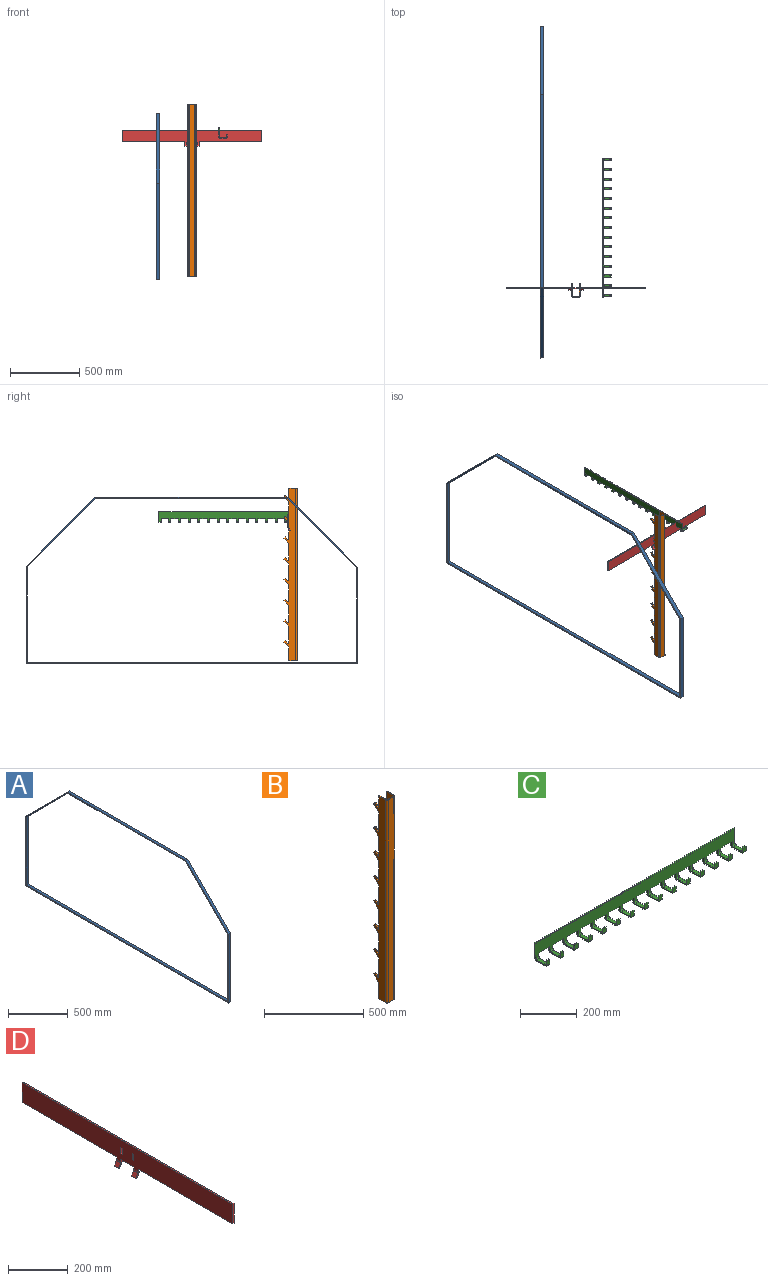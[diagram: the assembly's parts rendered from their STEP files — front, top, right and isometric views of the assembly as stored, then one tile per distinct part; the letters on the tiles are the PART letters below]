
ASSEMBLY  parts=4 mates=6
PART A: 14 faces, bbox 25x2400x1205 mm
  f0: plane 1397.07x25mm, normal (0,0,1), area 34926.8mm2, adj f1,f11,f12,f13
  f1: plane 505x505mm, normal (0,-0.71,0.71), area 17854.4mm2, adj f0,f2,f12,f13
  f2: plane 700x25mm, normal (0,-1,0), area 17500mm2, adj f1,f3,f12,f13
  f3: plane 2400x25mm, normal (0,0,-1), area 60000mm2, adj f2,f4,f12,f13
  f4: plane 707.07x25mm, normal (0,1,0), area 17676.8mm2, adj f3,f11,f12,f13
  f5: plane 2380x25mm, normal (0,0,1), area 59500mm2, adj f6,f10,f12,f13
  f6: plane 685.86x25mm, normal (0,1,0), area 17146.4mm2, adj f5,f7,f12,f13
  f7: plane 499.14x499.14mm, normal (0,0.71,-0.71), area 17647.3mm2, adj f6,f8,f12,f13
  f8: plane 1388.79x25mm, normal (0,0,-1), area 34719.7mm2, adj f7,f9,f12,f13
  f9: plane 492.07x492.07mm, normal (0,-0.71,-0.71), area 17397.3mm2, adj f8,f10,f12,f13
  f10: plane 692.93x25mm, normal (0,-1,0), area 17323.2mm2, adj f5,f9,f12,f13
  f11: plane 497.93x497.93mm, normal (0,0.71,0.71), area 17604.4mm2, adj f0,f4,f12,f13
  f12: plane 2400x1205mm, normal (1,0,0), area 65859.3mm2, adj f0,f1,f2,f3,f4,f5,f6,f7
  f13: plane 2400x1205mm, normal (-1,0,0), area 65859.3mm2, adj f0,f1,f2,f3,f4,f5,f6,f7
PART B: 134 faces, bbox 60x95.4x1250 mm
  f0: plane 100.89x5mm, normal (0,1,0), area 504.4mm2, adj f18,f20,f29,f122
  f1: plane 100.89x5mm, normal (0,1,0), area 504.4mm2, adj f24,f26,f29,f116
  f2: plane 122.79x5mm, normal (0,1,0), area 613.9mm2, adj f18,f20,f110,f120
  f3: plane 122.79x5mm, normal (0,1,0), area 613.9mm2, adj f24,f26,f104,f115
  f4: plane 122.79x5mm, normal (0,1,0), area 613.9mm2, adj f18,f20,f98,f108
  f5: plane 122.79x5mm, normal (0,1,0), area 613.9mm2, adj f24,f26,f92,f103
  f6: plane 122.79x5mm, normal (0,1,0), area 613.9mm2, adj f18,f20,f86,f96
  f7: plane 122.79x5mm, normal (0,1,0), area 613.9mm2, adj f24,f26,f80,f91
  f8: plane 122.79x5mm, normal (0,1,0), area 613.9mm2, adj f18,f20,f74,f84
  f9: plane 122.79x5mm, normal (0,1,0), area 613.9mm2, adj f24,f26,f68,f79
  f10: plane 122.79x5mm, normal (0,1,0), area 613.9mm2, adj f18,f20,f62,f72
  f11: plane 122.79x5mm, normal (0,1,0), area 613.9mm2, adj f24,f26,f56,f67
  f12: plane 122.79x5mm, normal (0,1,0), area 613.9mm2, adj f18,f20,f50,f60
  f13: plane 122.79x5mm, normal (0,1,0), area 613.9mm2, adj f24,f26,f44,f55
  f14: plane 122.79x5mm, normal (0,1,0), area 613.9mm2, adj f18,f20,f38,f48
  f15: plane 122.79x5mm, normal (0,1,0), area 613.9mm2, adj f24,f26,f32,f43
  f16: plane 1250x40mm, normal (0,1,0), area 50000mm2, adj f17,f27,f28,f29
  f17: cylinder r=5mm len=1250mm, axis (0,0,-1), area 9817.5mm2, adj f16,f18,f28,f29
  f18: plane 1250x50mm, normal (1,0,0), area 62500mm2, adj f0,f2,f4,f6,f8,f10,f12,f14
  f19: plane 71.9x5mm, normal (0,1,0), area 359.5mm2, adj f18,f20,f28,f36
  f20: plane 1250x84.36mm, normal (-1,0,0), area 66472.5mm2, adj f0,f2,f4,f6,f8,f10,f12,f14
  f21: cylinder r=11mm len=1250mm, axis (0,0,-1), area 21598.4mm2, adj f20,f22,f28,f29
  f22: plane 1250x38mm, normal (0,-1,0), area 47500mm2, adj f21,f23,f28,f29
  f23: cylinder r=11mm len=1250mm, axis (0,0,-1), area 21598.4mm2, adj f22,f24,f28,f29
  f24: plane 1250x84.36mm, normal (1,0,0), area 66472.5mm2, adj f1,f3,f5,f7,f9,f11,f13,f15
  f25: plane 71.9x5mm, normal (0,1,0), area 359.5mm2, adj f24,f26,f28,f31
  f26: plane 1250x50mm, normal (-1,0,0), area 62500mm2, adj f1,f3,f5,f7,f9,f11,f13,f15
  f27: cylinder r=5mm len=1250mm, axis (0,0,-1), area 9817.5mm2, adj f16,f26,f28,f29
  f28: plane 60x60mm, normal (0,0,1), area 808.8mm2, adj f16,f17,f18,f19,f20,f21,f22,f23
  f29: plane 60x60mm, normal (0,0,-1), area 808.8mm2, adj f0,f1,f16,f17,f18,f20,f21,f22
  f30: plane 27.21x1mm, normal (0,-1,0), area 27.2mm2, adj f26,f31,f32,f35
  f31: plane 6x6mm, normal (0,0,1), area 36mm2, adj f24,f25,f30,f34,f35
  f32: plane 31.82x31.82mm, normal (0,0.71,-0.71), area 270mm2, adj f15,f24,f30,f35,f132
  f33: plane 6x3.54mm, normal (0,0.71,0.71), area 30mm2, adj f24,f35,f132,f133
  f34: plane 15.21x15.21mm, normal (0,-0.71,0.71), area 129.1mm2, adj f24,f31,f35,f133
  f35: plane 43.89x33.28mm, normal (-1,0,0), area 644.8mm2, adj f30,f31,f32,f33,f34,f132,f133
  f36: plane 6x6mm, normal (0,0,1), area 36mm2, adj f19,f20,f37,f40,f41
  f37: plane 27.21x1mm, normal (0,-1,0), area 27.2mm2, adj f18,f36,f38,f41
  f38: plane 31.82x31.82mm, normal (0,0.71,-0.71), area 270mm2, adj f14,f20,f37,f41,f130
  f39: plane 6x3.54mm, normal (0,0.71,0.71), area 30mm2, adj f20,f41,f130,f131
  f40: plane 15.21x15.21mm, normal (0,-0.71,0.71), area 129.1mm2, adj f20,f36,f41,f131
  f41: plane 43.89x33.28mm, normal (1,0,0), area 644.8mm2, adj f36,f37,f38,f39,f40,f130,f131
  f42: plane 27.21x1mm, normal (0,-1,0), area 27.2mm2, adj f26,f43,f44,f47
  f43: plane 6x6mm, normal (0,0,1), area 36mm2, adj f15,f24,f42,f46,f47
  f44: plane 31.82x31.82mm, normal (0,0.71,-0.71), area 270mm2, adj f13,f24,f42,f47,f128
  f45: plane 6x3.54mm, normal (0,0.71,0.71), area 30mm2, adj f24,f47,f128,f129
  f46: plane 15.21x15.21mm, normal (0,-0.71,0.71), area 129.1mm2, adj f24,f43,f47,f129
  f47: plane 43.89x33.28mm, normal (-1,0,0), area 644.8mm2, adj f42,f43,f44,f45,f46,f128,f129
  f48: plane 6x6mm, normal (0,0,1), area 36mm2, adj f14,f20,f49,f52,f53
  f49: plane 27.21x1mm, normal (0,-1,0), area 27.2mm2, adj f18,f48,f50,f53
  f50: plane 31.82x31.82mm, normal (0,0.71,-0.71), area 270mm2, adj f12,f20,f49,f53,f126
  f51: plane 6x3.54mm, normal (0,0.71,0.71), area 30mm2, adj f20,f53,f126,f127
  f52: plane 15.21x15.21mm, normal (0,-0.71,0.71), area 129.1mm2, adj f20,f48,f53,f127
  f53: plane 43.89x33.28mm, normal (1,0,0), area 644.8mm2, adj f48,f49,f50,f51,f52,f126,f127
  f54: plane 27.21x1mm, normal (0,-1,0), area 27.2mm2, adj f26,f55,f56,f59
  f55: plane 6x6mm, normal (0,0,1), area 36mm2, adj f13,f24,f54,f58,f59
  f56: plane 35.36x35.36mm, normal (0,0.71,-0.71), area 300mm2, adj f11,f24,f54,f57,f59
  f57: plane 10.61x10.61mm, normal (0,0.71,0.71), area 90mm2, adj f24,f56,f58,f59
  f58: plane 18.75x18.75mm, normal (0,-0.71,0.71), area 159.1mm2, adj f24,f55,f57,f59
  f59: plane 45.96x35.36mm, normal (-1,0,0), area 655.5mm2, adj f54,f55,f56,f57,f58
  f60: plane 6x6mm, normal (0,0,1), area 36mm2, adj f12,f20,f61,f64,f65
  f61: plane 27.21x1mm, normal (0,-1,0), area 27.2mm2, adj f18,f60,f62,f65
  f62: plane 35.36x35.36mm, normal (0,0.71,-0.71), area 300mm2, adj f10,f20,f61,f63,f65
  f63: plane 10.61x10.61mm, normal (0,0.71,0.71), area 90mm2, adj f20,f62,f64,f65
  f64: plane 18.75x18.75mm, normal (0,-0.71,0.71), area 159.1mm2, adj f20,f60,f63,f65
  f65: plane 45.96x35.36mm, normal (1,0,0), area 655.5mm2, adj f60,f61,f62,f63,f64
  f66: plane 27.21x1mm, normal (0,-1,0), area 27.2mm2, adj f26,f67,f68,f71
  f67: plane 6x6mm, normal (0,0,1), area 36mm2, adj f11,f24,f66,f70,f71
  f68: plane 35.36x35.36mm, normal (0,0.71,-0.71), area 300mm2, adj f9,f24,f66,f69,f71
  f69: plane 10.61x10.61mm, normal (0,0.71,0.71), area 90mm2, adj f24,f68,f70,f71
  f70: plane 18.75x18.75mm, normal (0,-0.71,0.71), area 159.1mm2, adj f24,f67,f69,f71
  f71: plane 45.96x35.36mm, normal (-1,0,0), area 655.5mm2, adj f66,f67,f68,f69,f70
  f72: plane 6x6mm, normal (0,0,1), area 36mm2, adj f10,f20,f73,f76,f77
  f73: plane 27.21x1mm, normal (0,-1,0), area 27.2mm2, adj f18,f72,f74,f77
  f74: plane 35.36x35.36mm, normal (0,0.71,-0.71), area 300mm2, adj f8,f20,f73,f75,f77
  f75: plane 10.61x10.61mm, normal (0,0.71,0.71), area 90mm2, adj f20,f74,f76,f77
  f76: plane 18.75x18.75mm, normal (0,-0.71,0.71), area 159.1mm2, adj f20,f72,f75,f77
  f77: plane 45.96x35.36mm, normal (1,0,0), area 655.5mm2, adj f72,f73,f74,f75,f76
  f78: plane 27.21x1mm, normal (0,-1,0), area 27.2mm2, adj f26,f79,f80,f83
  f79: plane 6x6mm, normal (0,0,1), area 36mm2, adj f9,f24,f78,f82,f83
  f80: plane 35.36x35.36mm, normal (0,0.71,-0.71), area 300mm2, adj f7,f24,f78,f81,f83
  f81: plane 10.61x10.61mm, normal (0,0.71,0.71), area 90mm2, adj f24,f80,f82,f83
  f82: plane 18.75x18.75mm, normal (0,-0.71,0.71), area 159.1mm2, adj f24,f79,f81,f83
  f83: plane 45.96x35.36mm, normal (-1,0,0), area 655.5mm2, adj f78,f79,f80,f81,f82
  f84: plane 6x6mm, normal (0,0,1), area 36mm2, adj f8,f20,f85,f88,f89
  f85: plane 27.21x1mm, normal (0,-1,0), area 27.2mm2, adj f18,f84,f86,f89
  f86: plane 35.36x35.36mm, normal (0,0.71,-0.71), area 300mm2, adj f6,f20,f85,f87,f89
  f87: plane 10.61x10.61mm, normal (0,0.71,0.71), area 90mm2, adj f20,f86,f88,f89
  f88: plane 18.75x18.75mm, normal (0,-0.71,0.71), area 159.1mm2, adj f20,f84,f87,f89
  f89: plane 45.96x35.36mm, normal (1,0,0), area 655.5mm2, adj f84,f85,f86,f87,f88
  f90: plane 27.21x1mm, normal (0,-1,0), area 27.2mm2, adj f26,f91,f92,f95
  f91: plane 6x6mm, normal (0,0,1), area 36mm2, adj f7,f24,f90,f94,f95
  f92: plane 35.36x35.36mm, normal (0,0.71,-0.71), area 300mm2, adj f5,f24,f90,f93,f95
  f93: plane 10.61x10.61mm, normal (0,0.71,0.71), area 90mm2, adj f24,f92,f94,f95
  f94: plane 18.75x18.75mm, normal (0,-0.71,0.71), area 159.1mm2, adj f24,f91,f93,f95
  f95: plane 45.96x35.36mm, normal (-1,0,0), area 655.5mm2, adj f90,f91,f92,f93,f94
  f96: plane 6x6mm, normal (0,0,1), area 36mm2, adj f6,f20,f97,f100,f101
  f97: plane 27.21x1mm, normal (0,-1,0), area 27.2mm2, adj f18,f96,f98,f101
  f98: plane 35.36x35.36mm, normal (0,0.71,-0.71), area 300mm2, adj f4,f20,f97,f99,f101
  f99: plane 10.61x10.61mm, normal (0,0.71,0.71), area 90mm2, adj f20,f98,f100,f101
  f100: plane 18.75x18.75mm, normal (0,-0.71,0.71), area 159.1mm2, adj f20,f96,f99,f101
  f101: plane 45.96x35.36mm, normal (1,0,0), area 655.5mm2, adj f96,f97,f98,f99,f100
  f102: plane 27.21x1mm, normal (0,-1,0), area 27.2mm2, adj f26,f103,f104,f107
  f103: plane 6x6mm, normal (0,0,1), area 36mm2, adj f5,f24,f102,f106,f107
  f104: plane 35.36x35.36mm, normal (0,0.71,-0.71), area 300mm2, adj f3,f24,f102,f105,f107
  f105: plane 10.61x10.61mm, normal (0,0.71,0.71), area 90mm2, adj f24,f104,f106,f107
  f106: plane 18.75x18.75mm, normal (0,-0.71,0.71), area 159.1mm2, adj f24,f103,f105,f107
  f107: plane 45.96x35.36mm, normal (-1,0,0), area 655.5mm2, adj f102,f103,f104,f105,f106
  f108: plane 6x6mm, normal (0,0,1), area 36mm2, adj f4,f20,f109,f112,f113
  f109: plane 27.21x1mm, normal (0,-1,0), area 27.2mm2, adj f18,f108,f110,f113
  f110: plane 35.36x35.36mm, normal (0,0.71,-0.71), area 300mm2, adj f2,f20,f109,f111,f113
  f111: plane 10.61x10.61mm, normal (0,0.71,0.71), area 90mm2, adj f20,f110,f112,f113
  f112: plane 18.75x18.75mm, normal (0,-0.71,0.71), area 159.1mm2, adj f20,f108,f111,f113
  f113: plane 45.96x35.36mm, normal (1,0,0), area 655.5mm2, adj f108,f109,f110,f111,f112
  f114: plane 27.21x1mm, normal (0,-1,0), area 27.2mm2, adj f26,f115,f116,f119
  f115: plane 6x6mm, normal (0,0,1), area 36mm2, adj f3,f24,f114,f118,f119
  f116: plane 35.36x35.36mm, normal (0,0.71,-0.71), area 300mm2, adj f1,f24,f114,f117,f119
  f117: plane 10.61x10.61mm, normal (0,0.71,0.71), area 90mm2, adj f24,f116,f118,f119
  f118: plane 18.75x18.75mm, normal (0,-0.71,0.71), area 159.1mm2, adj f24,f115,f117,f119
  f119: plane 45.96x35.36mm, normal (-1,0,0), area 655.5mm2, adj f114,f115,f116,f117,f118
  f120: plane 6x6mm, normal (0,0,1), area 36mm2, adj f2,f20,f121,f124,f125
  f121: plane 27.21x1mm, normal (0,-1,0), area 27.2mm2, adj f18,f120,f122,f125
  f122: plane 35.36x35.36mm, normal (0,0.71,-0.71), area 300mm2, adj f0,f20,f121,f123,f125
  f123: plane 10.61x10.61mm, normal (0,0.71,0.71), area 90mm2, adj f20,f122,f124,f125
  f124: plane 18.75x18.75mm, normal (0,-0.71,0.71), area 159.1mm2, adj f20,f120,f123,f125
  f125: plane 45.96x35.36mm, normal (1,0,0), area 655.5mm2, adj f120,f121,f122,f123,f124
  f126: cylinder r=5mm len=7.07mm, axis (1,0,0), area 47.1mm2, adj f20,f50,f51,f53
  f127: cylinder r=5mm len=7.07mm, axis (1,0,0), area 47.1mm2, adj f20,f51,f52,f53
  f128: cylinder r=5mm len=7.07mm, axis (1,0,0), area 47.1mm2, adj f24,f44,f45,f47
  f129: cylinder r=5mm len=7.07mm, axis (1,0,0), area 47.1mm2, adj f24,f45,f46,f47
  f130: cylinder r=5mm len=7.07mm, axis (1,0,0), area 47.1mm2, adj f20,f38,f39,f41
  f131: cylinder r=5mm len=7.07mm, axis (1,0,0), area 47.1mm2, adj f20,f39,f40,f41
  f132: cylinder r=5mm len=7.07mm, axis (1,0,0), area 47.1mm2, adj f24,f32,f33,f35
  f133: cylinder r=5mm len=7.07mm, axis (1,0,0), area 47.1mm2, adj f24,f33,f34,f35
PART C: 184 faces, bbox 1000x60x75 mm
  f0: plane 5x5mm, normal (0,0,-1), area 25mm2, adj f16,f18,f19,f182
  f1: plane 55x5mm, normal (0,0,-1), area 275mm2, adj f18,f19,f171,f183
  f2: plane 55x5mm, normal (0,0,-1), area 275mm2, adj f18,f19,f160,f172
  f3: plane 55x5mm, normal (0,0,-1), area 275mm2, adj f18,f19,f149,f161
  f4: plane 55x5mm, normal (0,0,-1), area 275mm2, adj f18,f19,f138,f150
  f5: plane 55x5mm, normal (0,0,-1), area 275mm2, adj f18,f19,f127,f139
  f6: plane 55x5mm, normal (0,0,-1), area 275mm2, adj f18,f19,f116,f128
  f7: plane 55x5mm, normal (0,0,-1), area 275mm2, adj f18,f19,f105,f117
  f8: plane 55x5mm, normal (0,0,-1), area 275mm2, adj f18,f19,f94,f106
  f9: plane 55x5mm, normal (0,0,-1), area 275mm2, adj f18,f19,f83,f95
  f10: plane 55x5mm, normal (0,0,-1), area 275mm2, adj f18,f19,f72,f84
  f11: plane 55x5mm, normal (0,0,-1), area 275mm2, adj f18,f19,f61,f73
  f12: plane 55x5mm, normal (0,0,-1), area 275mm2, adj f18,f19,f50,f62
  f13: plane 55x5mm, normal (0,0,-1), area 275mm2, adj f18,f19,f39,f51
  f14: plane 55x5mm, normal (0,0,-1), area 275mm2, adj f18,f19,f29,f40
  f15: plane 1000x5mm, normal (0,0,1), area 5000mm2, adj f16,f17,f18,f19
  f16: plane 50x5mm, normal (-1,0,0), area 250mm2, adj f0,f15,f18,f19
  f17: plane 75x60mm, normal (1,0,0), area 750mm2, adj f15,f18,f19,f20,f21,f22,f23,f24
  f18: plane 1000x65mm, normal (0,-1,0), area 53375mm2, adj f0,f1,f2,f3,f4,f5,f6,f7
  f19: plane 1000x70mm, normal (0,1,0), area 54500mm2, adj f0,f1,f2,f3,f4,f5,f6,f7
  f20: cylinder r=5mm len=15mm, axis (1,0,0), area 117.8mm2, adj f17,f19,f28,f29
  f21: cylinder r=5mm len=15mm, axis (1,0,0), area 117.8mm2, adj f17,f18,f22,f29
  f22: plane 40x15mm, normal (0,0,1), area 600mm2, adj f17,f21,f23,f29
  f23: cylinder r=5mm len=15mm, axis (1,0,0), area 117.8mm2, adj f17,f22,f24,f29
  f24: plane 15x15mm, normal (0,1,0), area 225mm2, adj f17,f23,f25,f29
  f25: plane 15x5mm, normal (0,0,1), area 75mm2, adj f17,f24,f26,f29
  f26: plane 20x15mm, normal (0,-1,0), area 300mm2, adj f17,f25,f27,f29
  f27: cylinder r=5mm len=15mm, axis (1,0,0), area 117.8mm2, adj f17,f26,f28,f29
  f28: plane 50x15mm, normal (0,0,-1), area 750mm2, adj f17,f20,f27,f29
  f29: plane 60x25mm, normal (-1,0,0), area 500mm2, adj f14,f18,f19,f20,f21,f22,f23,f24
  f30: cylinder r=5mm len=15mm, axis (1,0,0), area 117.8mm2, adj f19,f38,f39,f40
  f31: cylinder r=5mm len=15mm, axis (1,0,0), area 117.8mm2, adj f18,f32,f39,f40
  f32: plane 40x15mm, normal (0,0,1), area 600mm2, adj f31,f33,f39,f40
  f33: cylinder r=5mm len=15mm, axis (1,0,0), area 117.8mm2, adj f32,f34,f39,f40
  f34: plane 15x15mm, normal (0,1,0), area 225mm2, adj f33,f35,f39,f40
  f35: plane 15x5mm, normal (0,0,1), area 75mm2, adj f34,f36,f39,f40
  f36: plane 20x15mm, normal (0,-1,0), area 300mm2, adj f35,f37,f39,f40
  f37: cylinder r=5mm len=15mm, axis (1,0,0), area 117.8mm2, adj f36,f38,f39,f40
  f38: plane 50x15mm, normal (0,0,-1), area 750mm2, adj f30,f37,f39,f40
  f39: plane 60x25mm, normal (-1,0,0), area 500mm2, adj f13,f18,f19,f30,f31,f32,f33,f34
  f40: plane 60x25mm, normal (1,0,0), area 500mm2, adj f14,f18,f19,f30,f31,f32,f33,f34
  f41: cylinder r=5mm len=15mm, axis (1,0,0), area 117.8mm2, adj f19,f49,f50,f51
  f42: cylinder r=5mm len=15mm, axis (1,0,0), area 117.8mm2, adj f18,f43,f50,f51
  f43: plane 40x15mm, normal (0,0,1), area 600mm2, adj f42,f44,f50,f51
  f44: cylinder r=5mm len=15mm, axis (1,0,0), area 117.8mm2, adj f43,f45,f50,f51
  f45: plane 15x15mm, normal (0,1,0), area 225mm2, adj f44,f46,f50,f51
  f46: plane 15x5mm, normal (0,0,1), area 75mm2, adj f45,f47,f50,f51
  f47: plane 20x15mm, normal (0,-1,0), area 300mm2, adj f46,f48,f50,f51
  f48: cylinder r=5mm len=15mm, axis (1,0,0), area 117.8mm2, adj f47,f49,f50,f51
  f49: plane 50x15mm, normal (0,0,-1), area 750mm2, adj f41,f48,f50,f51
  f50: plane 60x25mm, normal (-1,0,0), area 500mm2, adj f12,f18,f19,f41,f42,f43,f44,f45
  f51: plane 60x25mm, normal (1,0,0), area 500mm2, adj f13,f18,f19,f41,f42,f43,f44,f45
  f52: cylinder r=5mm len=15mm, axis (1,0,0), area 117.8mm2, adj f19,f60,f61,f62
  f53: cylinder r=5mm len=15mm, axis (1,0,0), area 117.8mm2, adj f18,f54,f61,f62
  f54: plane 40x15mm, normal (0,0,1), area 600mm2, adj f53,f55,f61,f62
  f55: cylinder r=5mm len=15mm, axis (1,0,0), area 117.8mm2, adj f54,f56,f61,f62
  f56: plane 15x15mm, normal (0,1,0), area 225mm2, adj f55,f57,f61,f62
  f57: plane 15x5mm, normal (0,0,1), area 75mm2, adj f56,f58,f61,f62
  f58: plane 20x15mm, normal (0,-1,0), area 300mm2, adj f57,f59,f61,f62
  f59: cylinder r=5mm len=15mm, axis (1,0,0), area 117.8mm2, adj f58,f60,f61,f62
  f60: plane 50x15mm, normal (0,0,-1), area 750mm2, adj f52,f59,f61,f62
  f61: plane 60x25mm, normal (-1,0,0), area 500mm2, adj f11,f18,f19,f52,f53,f54,f55,f56
  f62: plane 60x25mm, normal (1,0,0), area 500mm2, adj f12,f18,f19,f52,f53,f54,f55,f56
  f63: cylinder r=5mm len=15mm, axis (1,0,0), area 117.8mm2, adj f19,f71,f72,f73
  f64: cylinder r=5mm len=15mm, axis (1,0,0), area 117.8mm2, adj f18,f65,f72,f73
  f65: plane 40x15mm, normal (0,0,1), area 600mm2, adj f64,f66,f72,f73
  f66: cylinder r=5mm len=15mm, axis (1,0,0), area 117.8mm2, adj f65,f67,f72,f73
  f67: plane 15x15mm, normal (0,1,0), area 225mm2, adj f66,f68,f72,f73
  f68: plane 15x5mm, normal (0,0,1), area 75mm2, adj f67,f69,f72,f73
  f69: plane 20x15mm, normal (0,-1,0), area 300mm2, adj f68,f70,f72,f73
  f70: cylinder r=5mm len=15mm, axis (1,0,0), area 117.8mm2, adj f69,f71,f72,f73
  f71: plane 50x15mm, normal (0,0,-1), area 750mm2, adj f63,f70,f72,f73
  f72: plane 60x25mm, normal (-1,0,0), area 500mm2, adj f10,f18,f19,f63,f64,f65,f66,f67
  f73: plane 60x25mm, normal (1,0,0), area 500mm2, adj f11,f18,f19,f63,f64,f65,f66,f67
  f74: cylinder r=5mm len=15mm, axis (1,0,0), area 117.8mm2, adj f19,f82,f83,f84
  f75: cylinder r=5mm len=15mm, axis (1,0,0), area 117.8mm2, adj f18,f76,f83,f84
  f76: plane 40x15mm, normal (0,0,1), area 600mm2, adj f75,f77,f83,f84
  f77: cylinder r=5mm len=15mm, axis (1,0,0), area 117.8mm2, adj f76,f78,f83,f84
  f78: plane 15x15mm, normal (0,1,0), area 225mm2, adj f77,f79,f83,f84
  f79: plane 15x5mm, normal (0,0,1), area 75mm2, adj f78,f80,f83,f84
  f80: plane 20x15mm, normal (0,-1,0), area 300mm2, adj f79,f81,f83,f84
  f81: cylinder r=5mm len=15mm, axis (1,0,0), area 117.8mm2, adj f80,f82,f83,f84
  f82: plane 50x15mm, normal (0,0,-1), area 750mm2, adj f74,f81,f83,f84
  f83: plane 60x25mm, normal (-1,0,0), area 500mm2, adj f9,f18,f19,f74,f75,f76,f77,f78
  f84: plane 60x25mm, normal (1,0,0), area 500mm2, adj f10,f18,f19,f74,f75,f76,f77,f78
  f85: cylinder r=5mm len=15mm, axis (1,0,0), area 117.8mm2, adj f19,f93,f94,f95
  f86: cylinder r=5mm len=15mm, axis (1,0,0), area 117.8mm2, adj f18,f87,f94,f95
  f87: plane 40x15mm, normal (0,0,1), area 600mm2, adj f86,f88,f94,f95
  f88: cylinder r=5mm len=15mm, axis (1,0,0), area 117.8mm2, adj f87,f89,f94,f95
  f89: plane 15x15mm, normal (0,1,0), area 225mm2, adj f88,f90,f94,f95
  f90: plane 15x5mm, normal (0,0,1), area 75mm2, adj f89,f91,f94,f95
  f91: plane 20x15mm, normal (0,-1,0), area 300mm2, adj f90,f92,f94,f95
  f92: cylinder r=5mm len=15mm, axis (1,0,0), area 117.8mm2, adj f91,f93,f94,f95
  f93: plane 50x15mm, normal (0,0,-1), area 750mm2, adj f85,f92,f94,f95
  f94: plane 60x25mm, normal (-1,0,0), area 500mm2, adj f8,f18,f19,f85,f86,f87,f88,f89
  f95: plane 60x25mm, normal (1,0,0), area 500mm2, adj f9,f18,f19,f85,f86,f87,f88,f89
  f96: cylinder r=5mm len=15mm, axis (1,0,0), area 117.8mm2, adj f19,f104,f105,f106
  f97: cylinder r=5mm len=15mm, axis (1,0,0), area 117.8mm2, adj f18,f98,f105,f106
  f98: plane 40x15mm, normal (0,0,1), area 600mm2, adj f97,f99,f105,f106
  f99: cylinder r=5mm len=15mm, axis (1,0,0), area 117.8mm2, adj f98,f100,f105,f106
  f100: plane 15x15mm, normal (0,1,0), area 225mm2, adj f99,f101,f105,f106
  f101: plane 15x5mm, normal (0,0,1), area 75mm2, adj f100,f102,f105,f106
  f102: plane 20x15mm, normal (0,-1,0), area 300mm2, adj f101,f103,f105,f106
  f103: cylinder r=5mm len=15mm, axis (1,0,0), area 117.8mm2, adj f102,f104,f105,f106
  f104: plane 50x15mm, normal (0,0,-1), area 750mm2, adj f96,f103,f105,f106
  f105: plane 60x25mm, normal (-1,0,0), area 500mm2, adj f7,f18,f19,f96,f97,f98,f99,f100
  f106: plane 60x25mm, normal (1,0,0), area 500mm2, adj f8,f18,f19,f96,f97,f98,f99,f100
  f107: cylinder r=5mm len=15mm, axis (1,0,0), area 117.8mm2, adj f19,f115,f116,f117
  f108: cylinder r=5mm len=15mm, axis (1,0,0), area 117.8mm2, adj f18,f109,f116,f117
  f109: plane 40x15mm, normal (0,0,1), area 600mm2, adj f108,f110,f116,f117
  f110: cylinder r=5mm len=15mm, axis (1,0,0), area 117.8mm2, adj f109,f111,f116,f117
  f111: plane 15x15mm, normal (0,1,0), area 225mm2, adj f110,f112,f116,f117
  f112: plane 15x5mm, normal (0,0,1), area 75mm2, adj f111,f113,f116,f117
  f113: plane 20x15mm, normal (0,-1,0), area 300mm2, adj f112,f114,f116,f117
  f114: cylinder r=5mm len=15mm, axis (1,0,0), area 117.8mm2, adj f113,f115,f116,f117
  f115: plane 50x15mm, normal (0,0,-1), area 750mm2, adj f107,f114,f116,f117
  f116: plane 60x25mm, normal (-1,0,0), area 500mm2, adj f6,f18,f19,f107,f108,f109,f110,f111
  f117: plane 60x25mm, normal (1,0,0), area 500mm2, adj f7,f18,f19,f107,f108,f109,f110,f111
  f118: cylinder r=5mm len=15mm, axis (1,0,0), area 117.8mm2, adj f19,f126,f127,f128
  f119: cylinder r=5mm len=15mm, axis (1,0,0), area 117.8mm2, adj f18,f120,f127,f128
  f120: plane 40x15mm, normal (0,0,1), area 600mm2, adj f119,f121,f127,f128
  f121: cylinder r=5mm len=15mm, axis (1,0,0), area 117.8mm2, adj f120,f122,f127,f128
  f122: plane 15x15mm, normal (0,1,0), area 225mm2, adj f121,f123,f127,f128
  f123: plane 15x5mm, normal (0,0,1), area 75mm2, adj f122,f124,f127,f128
  f124: plane 20x15mm, normal (0,-1,0), area 300mm2, adj f123,f125,f127,f128
  f125: cylinder r=5mm len=15mm, axis (1,0,0), area 117.8mm2, adj f124,f126,f127,f128
  f126: plane 50x15mm, normal (0,0,-1), area 750mm2, adj f118,f125,f127,f128
  f127: plane 60x25mm, normal (-1,0,0), area 500mm2, adj f5,f18,f19,f118,f119,f120,f121,f122
  f128: plane 60x25mm, normal (1,0,0), area 500mm2, adj f6,f18,f19,f118,f119,f120,f121,f122
  f129: cylinder r=5mm len=15mm, axis (1,0,0), area 117.8mm2, adj f19,f137,f138,f139
  f130: cylinder r=5mm len=15mm, axis (1,0,0), area 117.8mm2, adj f18,f131,f138,f139
  f131: plane 40x15mm, normal (0,0,1), area 600mm2, adj f130,f132,f138,f139
  f132: cylinder r=5mm len=15mm, axis (1,0,0), area 117.8mm2, adj f131,f133,f138,f139
  f133: plane 15x15mm, normal (0,1,0), area 225mm2, adj f132,f134,f138,f139
  f134: plane 15x5mm, normal (0,0,1), area 75mm2, adj f133,f135,f138,f139
  f135: plane 20x15mm, normal (0,-1,0), area 300mm2, adj f134,f136,f138,f139
  f136: cylinder r=5mm len=15mm, axis (1,0,0), area 117.8mm2, adj f135,f137,f138,f139
  f137: plane 50x15mm, normal (0,0,-1), area 750mm2, adj f129,f136,f138,f139
  f138: plane 60x25mm, normal (-1,0,0), area 500mm2, adj f4,f18,f19,f129,f130,f131,f132,f133
  f139: plane 60x25mm, normal (1,0,0), area 500mm2, adj f5,f18,f19,f129,f130,f131,f132,f133
  f140: cylinder r=5mm len=15mm, axis (1,0,0), area 117.8mm2, adj f19,f148,f149,f150
  f141: cylinder r=5mm len=15mm, axis (1,0,0), area 117.8mm2, adj f18,f142,f149,f150
  f142: plane 40x15mm, normal (0,0,1), area 600mm2, adj f141,f143,f149,f150
  f143: cylinder r=5mm len=15mm, axis (1,0,0), area 117.8mm2, adj f142,f144,f149,f150
  f144: plane 15x15mm, normal (0,1,0), area 225mm2, adj f143,f145,f149,f150
  f145: plane 15x5mm, normal (0,0,1), area 75mm2, adj f144,f146,f149,f150
  f146: plane 20x15mm, normal (0,-1,0), area 300mm2, adj f145,f147,f149,f150
  f147: cylinder r=5mm len=15mm, axis (1,0,0), area 117.8mm2, adj f146,f148,f149,f150
  f148: plane 50x15mm, normal (0,0,-1), area 750mm2, adj f140,f147,f149,f150
  f149: plane 60x25mm, normal (-1,0,0), area 500mm2, adj f3,f18,f19,f140,f141,f142,f143,f144
  f150: plane 60x25mm, normal (1,0,0), area 500mm2, adj f4,f18,f19,f140,f141,f142,f143,f144
  f151: cylinder r=5mm len=15mm, axis (1,0,0), area 117.8mm2, adj f19,f159,f160,f161
  f152: cylinder r=5mm len=15mm, axis (1,0,0), area 117.8mm2, adj f18,f153,f160,f161
  f153: plane 40x15mm, normal (0,0,1), area 600mm2, adj f152,f154,f160,f161
  f154: cylinder r=5mm len=15mm, axis (1,0,0), area 117.8mm2, adj f153,f155,f160,f161
  f155: plane 15x15mm, normal (0,1,0), area 225mm2, adj f154,f156,f160,f161
  f156: plane 15x5mm, normal (0,0,1), area 75mm2, adj f155,f157,f160,f161
  f157: plane 20x15mm, normal (0,-1,0), area 300mm2, adj f156,f158,f160,f161
  f158: cylinder r=5mm len=15mm, axis (1,0,0), area 117.8mm2, adj f157,f159,f160,f161
  f159: plane 50x15mm, normal (0,0,-1), area 750mm2, adj f151,f158,f160,f161
  f160: plane 60x25mm, normal (-1,0,0), area 500mm2, adj f2,f18,f19,f151,f152,f153,f154,f155
  f161: plane 60x25mm, normal (1,0,0), area 500mm2, adj f3,f18,f19,f151,f152,f153,f154,f155
  f162: cylinder r=5mm len=15mm, axis (1,0,0), area 117.8mm2, adj f19,f170,f171,f172
  f163: cylinder r=5mm len=15mm, axis (1,0,0), area 117.8mm2, adj f18,f164,f171,f172
  f164: plane 40x15mm, normal (0,0,1), area 600mm2, adj f163,f165,f171,f172
  f165: cylinder r=5mm len=15mm, axis (1,0,0), area 117.8mm2, adj f164,f166,f171,f172
  f166: plane 15x15mm, normal (0,1,0), area 225mm2, adj f165,f167,f171,f172
  f167: plane 15x5mm, normal (0,0,1), area 75mm2, adj f166,f168,f171,f172
  f168: plane 20x15mm, normal (0,-1,0), area 300mm2, adj f167,f169,f171,f172
  f169: cylinder r=5mm len=15mm, axis (1,0,0), area 117.8mm2, adj f168,f170,f171,f172
  f170: plane 50x15mm, normal (0,0,-1), area 750mm2, adj f162,f169,f171,f172
  f171: plane 60x25mm, normal (-1,0,0), area 500mm2, adj f1,f18,f19,f162,f163,f164,f165,f166
  f172: plane 60x25mm, normal (1,0,0), area 500mm2, adj f2,f18,f19,f162,f163,f164,f165,f166
  f173: cylinder r=5mm len=15mm, axis (1,0,0), area 117.8mm2, adj f19,f181,f182,f183
  f174: cylinder r=5mm len=15mm, axis (1,0,0), area 117.8mm2, adj f18,f175,f182,f183
  f175: plane 40x15mm, normal (0,0,1), area 600mm2, adj f174,f176,f182,f183
  f176: cylinder r=5mm len=15mm, axis (1,0,0), area 117.8mm2, adj f175,f177,f182,f183
  f177: plane 15x15mm, normal (0,1,0), area 225mm2, adj f176,f178,f182,f183
  f178: plane 15x5mm, normal (0,0,1), area 75mm2, adj f177,f179,f182,f183
  f179: plane 20x15mm, normal (0,-1,0), area 300mm2, adj f178,f180,f182,f183
  f180: cylinder r=5mm len=15mm, axis (1,0,0), area 117.8mm2, adj f179,f181,f182,f183
  f181: plane 50x15mm, normal (0,0,-1), area 750mm2, adj f173,f180,f182,f183
  f182: plane 60x25mm, normal (-1,0,0), area 500mm2, adj f0,f18,f19,f173,f174,f175,f176,f177
  f183: plane 60x25mm, normal (1,0,0), area 500mm2, adj f1,f18,f19,f173,f174,f175,f176,f177
PART D: 30 faces, bbox 17.3x1000x115.3 mm
  f0: plane 35.32x17.34mm, normal (0,1,0), area 220.8mm2, adj f1,f18,f19,f20,f21,f22,f23,f24
  f1: plane 62x6mm, normal (0,0,-1), area 372mm2, adj f0,f2,f18,f19
  f2: plane 35.32x17.34mm, normal (0,-1,0), area 220.8mm2, adj f1,f18,f19,f25,f26,f27,f28,f29
  f3: plane 35.32x17.34mm, normal (0,1,0), area 220.8mm2, adj f4,f18,f19,f25,f26,f27,f28,f29
  f4: plane 449x6mm, normal (0,0,-1), area 2694mm2, adj f3,f5,f18,f19
  f5: plane 80x6mm, normal (0,1,0), area 480mm2, adj f4,f6,f18,f19
  f6: plane 1000x6mm, normal (0,0,1), area 6000mm2, adj f5,f7,f18,f19
  f7: plane 80x6mm, normal (0,-1,0), area 480mm2, adj f6,f8,f18,f19
  f8: plane 449x6mm, normal (0,0,-1), area 2694mm2, adj f7,f9,f18,f19
  f9: plane 35.32x17.34mm, normal (0,-1,0), area 220.8mm2, adj f8,f18,f19,f20,f21,f22,f23,f24
  f10: plane 8x6mm, normal (0,0,1), area 48mm2, adj f11,f16,f18,f19
  f11: plane 25x6mm, normal (0,1,0), area 150mm2, adj f10,f12,f18,f19
  f12: plane 8x6mm, normal (0,0,-1), area 48mm2, adj f11,f16,f18,f19
  f13: plane 8x6mm, normal (0,0,1), area 48mm2, adj f14,f17,f18,f19
  f14: plane 25x6mm, normal (0,1,0), area 150mm2, adj f13,f15,f18,f19
  f15: plane 8x6mm, normal (0,0,-1), area 48mm2, adj f14,f17,f18,f19
  f16: plane 25x6mm, normal (0,-1,0), area 150mm2, adj f10,f12,f18,f19
  f17: plane 25x6mm, normal (0,-1,0), area 150mm2, adj f13,f15,f18,f19
  f18: plane 1000x90mm, normal (1,0,0), area 80000mm2, adj f0,f1,f2,f3,f4,f5,f6,f7
  f19: plane 1000x90mm, normal (-1,0,0), area 80000mm2, adj f0,f1,f2,f3,f4,f5,f6,f7
  f20: plane 20x17.32mm, normal (0.87,0,-0.5), area 400mm2, adj f0,f9,f21,f24
  f21: cylinder r=16mm len=20mm, axis (0,-1,0), area 167.6mm2, adj f0,f9,f18,f20
  f22: cylinder r=10mm len=20mm, axis (0,-1,0), area 104.7mm2, adj f0,f9,f19,f23
  f23: plane 20x17.32mm, normal (-0.87,0,0.5), area 400mm2, adj f0,f9,f22,f24
  f24: plane 20x5.2mm, normal (-0.5,0,-0.87), area 120mm2, adj f0,f9,f20,f23
  f25: plane 20x17.32mm, normal (0.87,0,-0.5), area 400mm2, adj f2,f3,f26,f29
  f26: cylinder r=16mm len=20mm, axis (0,-1,0), area 167.6mm2, adj f2,f3,f18,f25
  f27: cylinder r=10mm len=20mm, axis (0,-1,0), area 104.7mm2, adj f2,f3,f19,f28
  f28: plane 20x17.32mm, normal (-0.87,0,0.5), area 400mm2, adj f2,f3,f27,f29
  f29: plane 20x5.2mm, normal (-0.5,0,-0.87), area 120mm2, adj f2,f3,f25,f28
PLACE A rot(axis=(0,-1,0),0deg) t=(-245.83,-198.59,-268.44)mm
PLACE B t=(-1.73,241.32,-246.32)mm fixed
PLACE C rot(axis=(0,0,1),90deg) t=(193.38,240.25,781.78)mm
PLACE D rot(axis=(0,0,1),90deg) t=(-1.25,301.32,812.61)mm
MATE parallel B.f22 <-> A.f2  axis (0,-1,0) through (-1.73,241.32,-246.32)mm
MATE parallel D.f6 <-> B.f28  axis (0,0,1) through (-1.25,304.32,812.61)mm
MATE parallel C.f19 <-> D.f7  axis (-1,0,0) through (193.38,740.46,803.89)mm
MATE parallel C.f15 <-> D.f8  axis (0,0,1) through (195.88,740.25,831.78)mm
MATE planar D.f19 <-> B.f14  axis (0,-1,0) through (-1.25,301.32,772.4)mm
MATE parallel D.f0 <-> B.f24  axis (-1,0,0) through (29.75,299.98,717.61)mm
